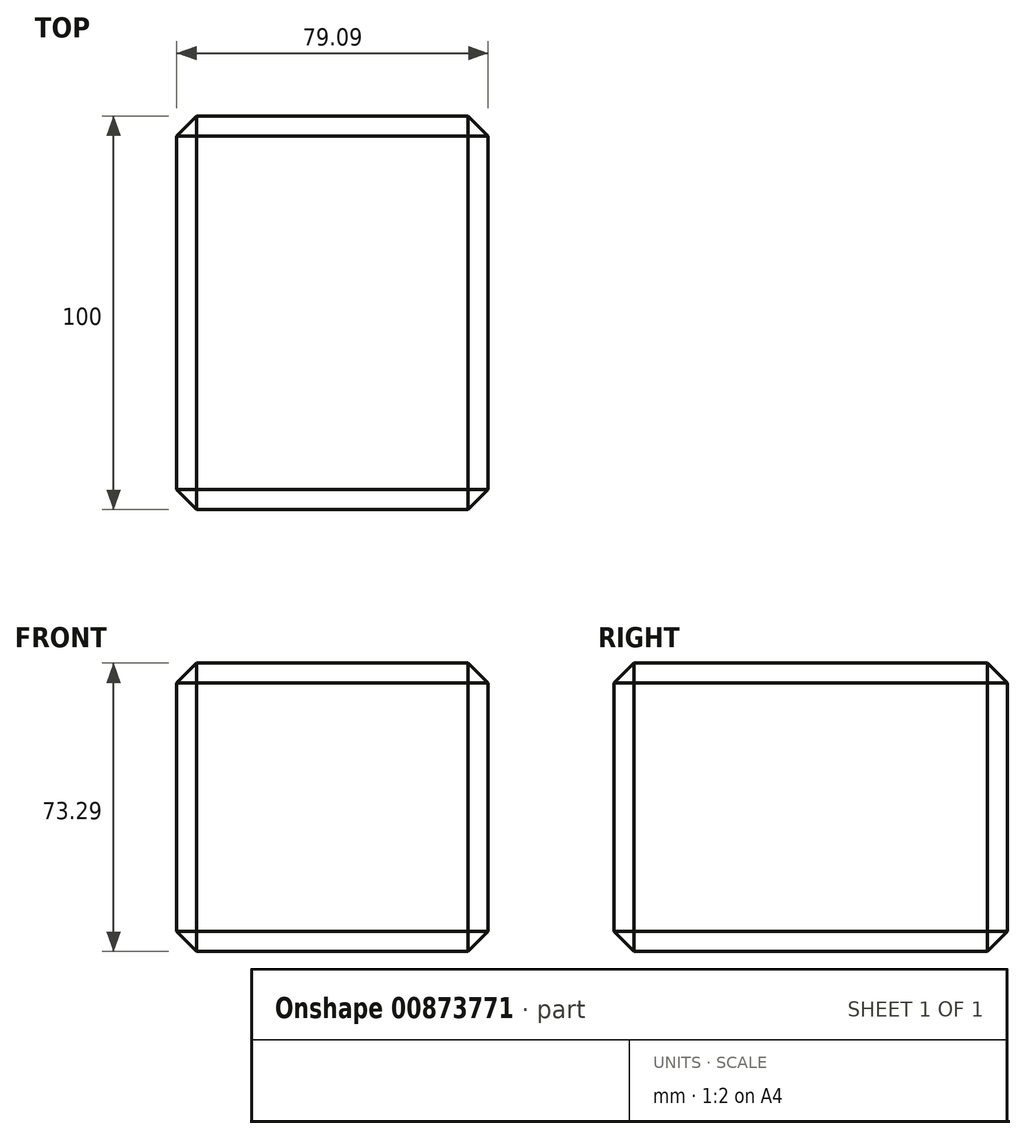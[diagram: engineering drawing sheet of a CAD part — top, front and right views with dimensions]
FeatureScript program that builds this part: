
annotation { "Feature Type Name" : "Feature", "Feature Type Description" : "" }
export const myFeature = defineFeature(function(context is Context, id is Id, definition is map)
    precondition{}
    {
        {
            var Q0;
            Q0=qCreatedBy(makeId("Front.planeOp"),FACE);
            var sketch = newSketch(context, id + "F0", { "sketchPlane" : qUnion([Q0])});
            skLineSegment(sketch, "E0.bottom", {"start": v(-37.4, 39.7) * mm, "end": v(41.68, 39.7) * mm});
            skLineSegment(sketch, "E0.top", {"start": v(-37.4, -33.6) * mm, "end": v(41.68, -33.6) * mm});
            skLineSegment(sketch, "E0.left", {"start": v(-37.4, 39.7) * mm, "end": v(-37.4, -33.6) * mm});
            skLineSegment(sketch, "E0.right", {"start": v(41.68, 39.7) * mm, "end": v(41.68, -33.6) * mm});
            skSolve(sketch);
        }
        {
            var Q0;
            Q0 = qSketchRegion(id + "F0", true);
            extrude(context, id + "F1", {"entities" : qUnion([Q0]), "endBound" : BoundingType.SYMMETRIC, "depth" : 100 * mm, "offsetDistance" : 25.4 * mm});
        }
        {
            var Q0;
            Q0=makeQuery(id+"F1.opExtrude","SWEPT_FACE",FACE,{"disambiguationData":[OSD([sQuery(id+"F0.wireOp",EDGE,"E0.bottom")])]});
            var Q1;
            Q1=makeQuery(id+"F1.opExtrude","CAP_FACE",FACE,{"disambiguationData":[OSD([sQuery(id+"F0.wireOp",EDGE,"E0.bottom"),sQuery(id+"F0.wireOp",EDGE,"E0.top"),sQuery(id+"F0.wireOp",EDGE,"E0.left"),sQuery(id+"F0.wireOp",EDGE,"E0.right")])],"isStart":false});
            var Q2;
            Q2=makeQuery(id+"F1.opExtrude","SWEPT_FACE",FACE,{"disambiguationData":[OSD([sQuery(id+"F0.wireOp",EDGE,"E0.right")])]});
            var Q3;
            Q3=makeQuery(id+"F1.opExtrude","SWEPT_FACE",FACE,{"disambiguationData":[OSD([sQuery(id+"F0.wireOp",EDGE,"E0.top")])]});
            var Q4;
            Q4=makeQuery(id+"F1.opExtrude","CAP_FACE",FACE,{"disambiguationData":[OSD([sQuery(id+"F0.wireOp",EDGE,"E0.bottom"),sQuery(id+"F0.wireOp",EDGE,"E0.top"),sQuery(id+"F0.wireOp",EDGE,"E0.left"),sQuery(id+"F0.wireOp",EDGE,"E0.right")])],"isStart":true});
            chamfer(context, id + "F2", {"entities" : qUnion([Q0, Q1, Q2, Q3, Q4]), "width" : 5.08 * mm, "tangentPropagation" : true});
        }
    });
